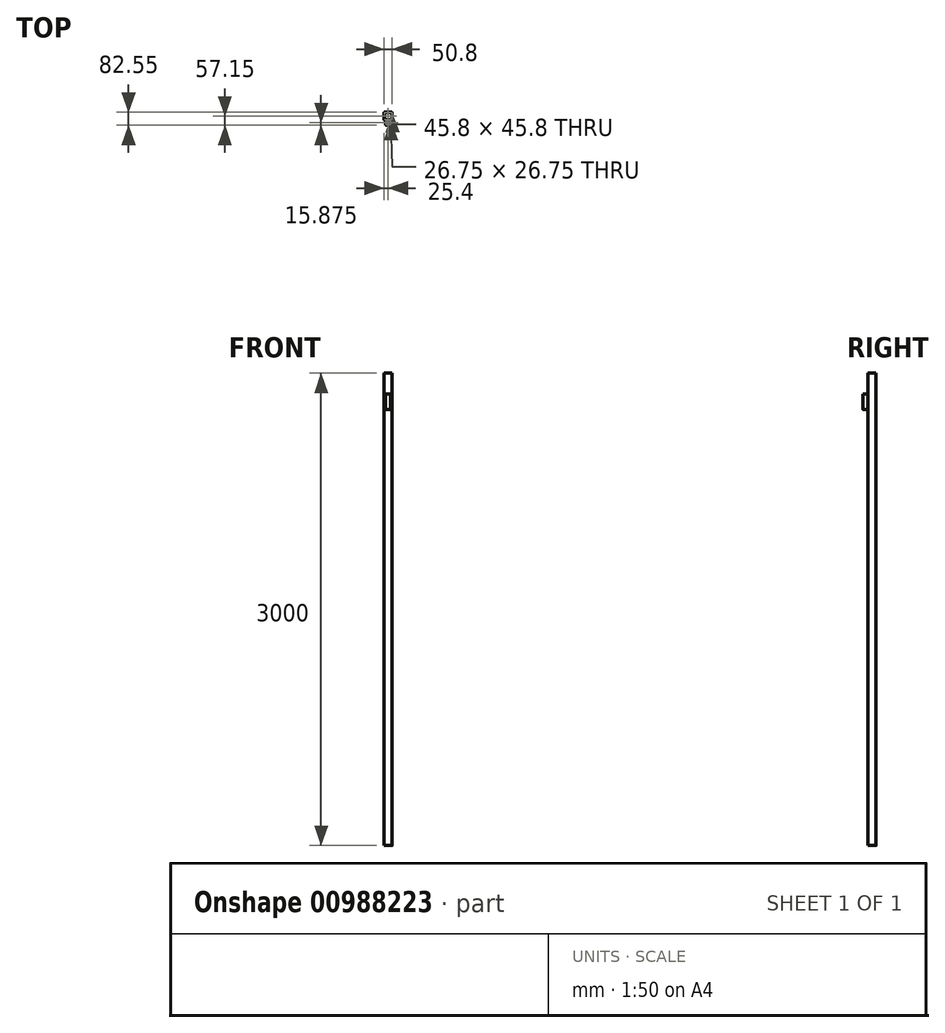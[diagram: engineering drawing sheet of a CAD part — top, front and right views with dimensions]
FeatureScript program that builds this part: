
annotation { "Feature Type Name" : "Feature", "Feature Type Description" : "" }
export const myFeature = defineFeature(function(context is Context, id is Id, definition is map)
    precondition{}
    {
        {
            var Q0;
            Q0=qCreatedBy(makeId("Top.planeOp"),FACE);
            var sketch = newSketch(context, id + "F0", { "sketchPlane" : qUnion([Q0])});
            skLineSegment(sketch, "E0.bottom", {"start": v(22.9, 25.4) * mm, "end": v(-22.9, 25.4) * mm});
            skLineSegment(sketch, "E0.top", {"start": v(22.9, -25.4) * mm, "end": v(-22.9, -25.4) * mm});
            skLineSegment(sketch, "E0.left", {"start": v(25.4, 22.9) * mm, "end": v(25.4, -22.9) * mm});
            skLineSegment(sketch, "E0.right", {"start": v(-25.4, 22.9) * mm, "end": v(-25.4, -22.9) * mm});
            skPoint(sketch, "E0.middle", {"position": v(0, 0) * mm});
            skPoint(sketch, "E1.visualSharp", {"position": v(25.4, 25.4) * mm});
            skArc(sketch, "E1.filletArc", {"start": v(25.4, 22.9) * mm, "mid": v(24.67, 24.67) * mm, "end": v(22.9, 25.4) * mm});
            skPoint(sketch, "E2.visualSharp", {"position": v(-25.4, 25.4) * mm});
            skArc(sketch, "E2.filletArc", {"start": v(-22.9, 25.4) * mm, "mid": v(-24.67, 24.67) * mm, "end": v(-25.4, 22.9) * mm});
            skPoint(sketch, "E3.visualSharp", {"position": v(-25.4, -25.4) * mm});
            skArc(sketch, "E3.filletArc", {"start": v(-25.4, -22.9) * mm, "mid": v(-24.67, -24.67) * mm, "end": v(-22.9, -25.4) * mm});
            skPoint(sketch, "E4.visualSharp", {"position": v(25.4, -25.4) * mm});
            skArc(sketch, "E4.filletArc", {"start": v(22.9, -25.4) * mm, "mid": v(24.67, -24.67) * mm, "end": v(25.4, -22.9) * mm});
            skLineSegment(sketch, "E5.0", {"start": v(22.9, 22.9) * mm, "end": v(22.9, 22.9) * mm});
            skLineSegment(sketch, "E5.1", {"start": v(22.9, 22.9) * mm, "end": v(22.9, -22.9) * mm});
            skLineSegment(sketch, "E5.2", {"start": v(22.9, 22.9) * mm, "end": v(-22.9, 22.9) * mm});
            skLineSegment(sketch, "E5.3", {"start": v(22.9, -22.9) * mm, "end": v(22.9, -22.9) * mm});
            skLineSegment(sketch, "E5.4", {"start": v(-22.9, 22.9) * mm, "end": v(-22.9, 22.9) * mm});
            skLineSegment(sketch, "E5.5", {"start": v(-22.9, 22.9) * mm, "end": v(-22.9, -22.9) * mm});
            skLineSegment(sketch, "E5.6", {"start": v(-22.9, -22.9) * mm, "end": v(-22.9, -22.9) * mm});
            skLineSegment(sketch, "E5.7", {"start": v(22.9, -22.9) * mm, "end": v(-22.9, -22.9) * mm});
            skSolve(sketch);
        }
        {
            var Q0;
            Q0=makeQuery(id+"F0.imprint","IMPRINT",FACE,{"disambiguationData":[TD([[makeQuery(id+"F0.imprint","IMPRINT",EDGE,{"derivedFrom":sQuery(id+"F0.wireOp",EDGE,"E0.bottom")}),1.0]])]});
            extrude(context, id + "F1", {"entities" : qUnion([Q0]), "depth" : 3000 * mm, "offsetDistance" : 25 * mm});
        }
        {
            var Q0;
            Q0=makeQuery(id+"F1.opExtrude","SWEPT_FACE",FACE,{"disambiguationData":[OSD([sQuery(id+"F0.wireOp",EDGE,"E0.top")])]});
            var sketch = newSketch(context, id + "F2", { "sketchPlane" : qUnion([Q0])});
            skLineSegment(sketch, "E6.bottom", {"start": v(15.88, 2868.25) * mm, "end": v(-15.87, 2868.25) * mm});
            skLineSegment(sketch, "E6.top", {"start": v(15.88, 2768.25) * mm, "end": v(-15.87, 2768.25) * mm});
            skLineSegment(sketch, "E6.left", {"start": v(15.88, 2868.25) * mm, "end": v(15.88, 2768.25) * mm});
            skLineSegment(sketch, "E6.right", {"start": v(-15.87, 2868.25) * mm, "end": v(-15.87, 2768.25) * mm});
            skPoint(sketch, "E6.middle", {"position": v(0, 2818.25) * mm});
            skSolve(sketch);
        }
        {
            var Q0;
            Q0=qSketchRegion(id+"F2",true);
            extrude(context, id + "F3", {"entities" : qUnion([Q0]), "operationType" : NewBodyOperationType.ADD, "depth" : 31.75 * mm, "offsetDistance" : 25 * mm});
        }
        {
            var Q0;
            Q0=makeQuery(id+"F3.opExtrude","CAP_EDGE",EDGE,{"disambiguationData":[OSD([sQuery(id+"F2.wireOp",EDGE,"E6.right")])],"isStart":false});
            var Q1;
            Q1=makeQuery(id+"F3.opExtrude","CAP_EDGE",EDGE,{"disambiguationData":[OSD([sQuery(id+"F2.wireOp",EDGE,"E6.left")])],"isStart":false});
            fillet(context, id + "F4", {"entities" : qUnion([Q0, Q1]), "radius" : 2.5 * mm, "tangentPropagation" : true, "allowEdgeOverflow" : false});
        }
        {
            var Q0;
            Q0=makeQuery(id+"F3.opExtrude","SWEPT_FACE",FACE,{"disambiguationData":[OSD([sQuery(id+"F2.wireOp",EDGE,"E6.bottom")])]});
            var sketch = newSketch(context, id + "F5", { "sketchPlane" : qUnion([Q0])});
            skLineSegment(sketch, "E7.0", {"start": v(13.38, -54.65) * mm, "end": v(13.38, -27.9) * mm});
            skLineSegment(sketch, "E7.1", {"start": v(-13.37, -54.65) * mm, "end": v(-13.37, -27.9) * mm});
            skLineSegment(sketch, "E7.2", {"start": v(-13.37, -54.65) * mm, "end": v(-13.37, -54.65) * mm});
            skLineSegment(sketch, "E7.3", {"start": v(13.38, -27.9) * mm, "end": v(-13.37, -27.9) * mm});
            skLineSegment(sketch, "E7.4", {"start": v(13.38, -54.65) * mm, "end": v(-13.37, -54.65) * mm});
            skLineSegment(sketch, "E7.5", {"start": v(13.38, -54.65) * mm, "end": v(13.38, -54.65) * mm});
            skSolve(sketch);
        }
        {
            var Q0;
            Q0=qSketchRegion(id+"F5",true);
            extrude(context, id + "F6", {"entities" : qUnion([Q0]), "operationType" : NewBodyOperationType.REMOVE, "endBound" : BoundingType.UP_TO_NEXT, "oppositeDirection" : true, "depth" : 25 * mm, "offsetDistance" : 25 * mm});
        }
        {
            var Q0;
            Q0=qCreatedBy(makeId("Front.planeOp"),FACE);
            var sketch = newSketch(context, id + "F7", { "sketchPlane" : qUnion([Q0])});
            skLineSegment(sketch, "E8", {"start": v(0, 0) * mm, "end": v(0, 52.75) * mm});
            skSolve(sketch);
        }
    });
